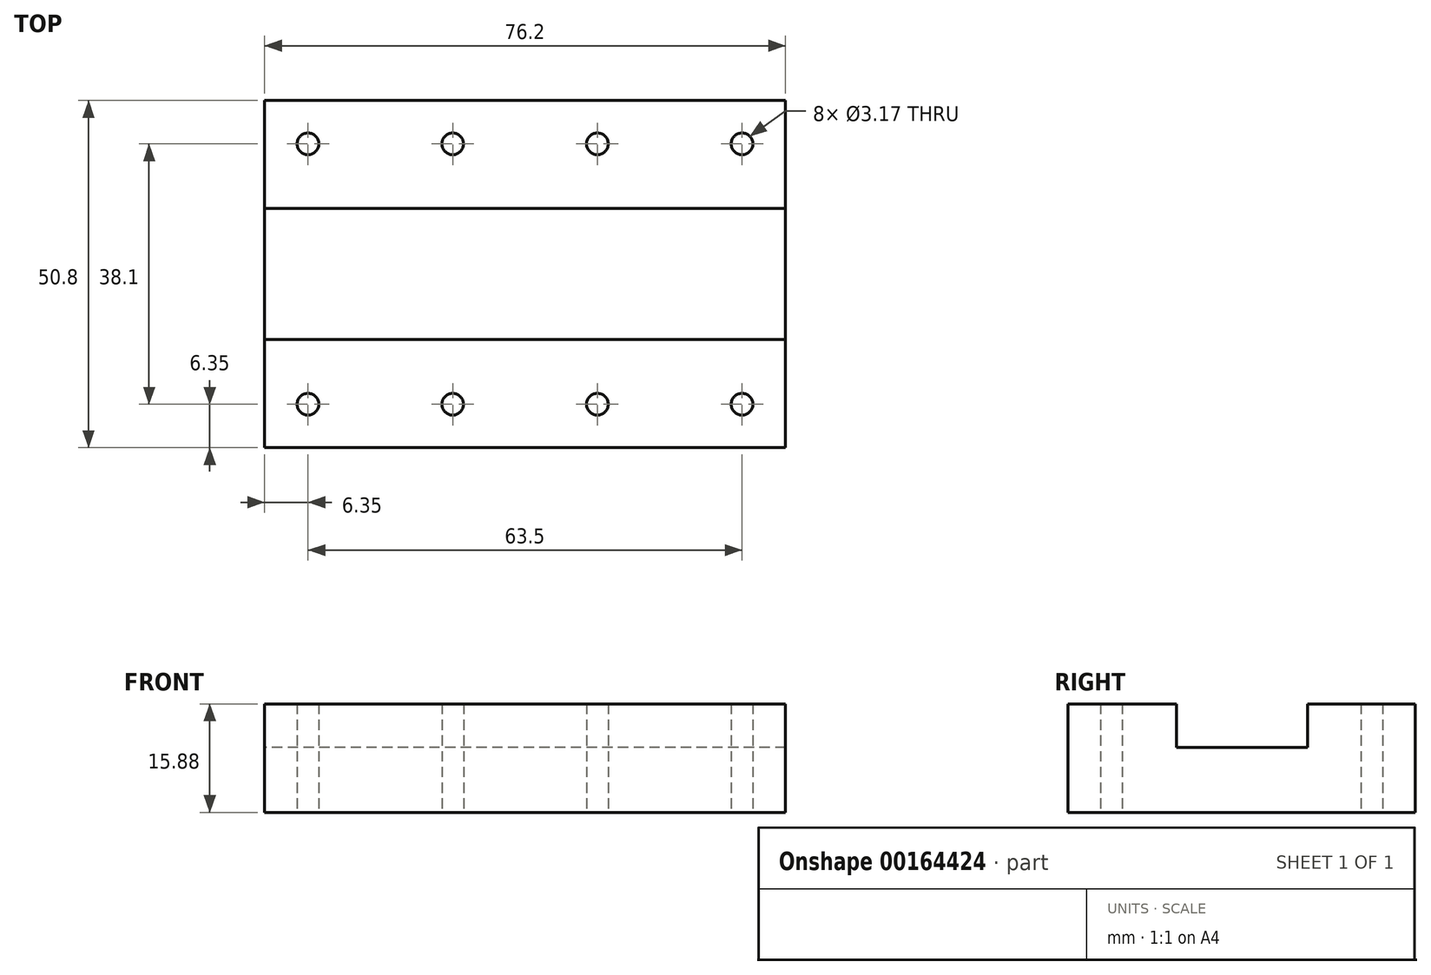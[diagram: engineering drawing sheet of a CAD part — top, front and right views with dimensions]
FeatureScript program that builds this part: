
annotation { "Feature Type Name" : "Feature", "Feature Type Description" : "" }
export const myFeature = defineFeature(function(context is Context, id is Id, definition is map)
    precondition{}
    {
        {
            var Q0;
            Q0=qCreatedBy(makeId("Top.planeOp"),FACE);
            var sketch = newSketch(context, id + "F0", { "sketchPlane" : qUnion([Q0])});
            skLineSegment(sketch, "E0.bottom", {"start": v(-38.1, -25.4) * mm, "end": v(38.1, -25.4) * mm});
            skLineSegment(sketch, "E0.top", {"start": v(-38.1, 25.4) * mm, "end": v(38.1, 25.4) * mm});
            skLineSegment(sketch, "E0.left", {"start": v(-38.1, -25.4) * mm, "end": v(-38.1, 25.4) * mm});
            skLineSegment(sketch, "E0.right", {"start": v(38.1, -25.4) * mm, "end": v(38.1, 25.4) * mm});
            skPoint(sketch, "E0.middle", {"position": v(0, 0) * mm});
            skLineSegment(sketch, "E1.bottom", {"start": v(-31.75, 19.05) * mm, "end": v(31.75, 19.05) * mm, "construction": true});
            skLineSegment(sketch, "E1.top", {"start": v(-31.75, -19.05) * mm, "end": v(31.75, -19.05) * mm, "construction": true});
            skLineSegment(sketch, "E1.left", {"start": v(-31.75, 19.05) * mm, "end": v(-31.75, -19.05) * mm, "construction": true});
            skLineSegment(sketch, "E1.right", {"start": v(31.75, 19.05) * mm, "end": v(31.75, -19.05) * mm, "construction": true});
            skCircle(sketch, "E2", {"center": v(-31.75, -19.05) * mm, "radius": 1.59 * mm});
            skCircle(sketch, "E3", {"center": v(-31.75, 19.05) * mm, "radius": 1.59 * mm});
            skCircle(sketch, "E4", {"center": v(31.75, 19.05) * mm, "radius": 1.59 * mm});
            skCircle(sketch, "E5", {"center": v(31.75, -19.05) * mm, "radius": 1.59 * mm});
            skCircle(sketch, "E6.1.0.0", {"center": v(-10.58, 19.05) * mm, "radius": 1.59 * mm});
            skCircle(sketch, "E6.1.0.1", {"center": v(-10.58, -19.05) * mm, "radius": 1.59 * mm});
            skCircle(sketch, "E6.2.0.0", {"center": v(10.58, 19.05) * mm, "radius": 1.59 * mm});
            skCircle(sketch, "E6.2.0.1", {"center": v(10.58, -19.05) * mm, "radius": 1.59 * mm});
            skLineSegment(sketch, "E6.direction1", {"start": v(-31.75, -19.05) * mm, "end": v(-10.58, -19.05) * mm, "construction": true});
            skLineSegment(sketch, "E7", {"start": v(0, 0) * mm, "end": v(-10.58, 0) * mm, "construction": true});
            skLineSegment(sketch, "E8", {"start": v(-10.58, 0) * mm, "end": v(-10.58, 19.05) * mm, "construction": true});
            skLineSegment(sketch, "E9", {"start": v(0, 0) * mm, "end": v(10.58, 0) * mm, "construction": true});
            skLineSegment(sketch, "E10", {"start": v(10.58, 0) * mm, "end": v(10.58, 19.05) * mm, "construction": true});
            skSolve(sketch);
        }
        {
            var Q0;
            Q0=makeQuery(id+"F0.imprint","IMPRINT",FACE,{"disambiguationData":[TD([[makeQuery(id+"F0.imprint","IMPRINT",EDGE,{"derivedFrom":sQuery(id+"F0.wireOp",EDGE,"E0.bottom")}),1.0]])]});
            extrude(context, id + "F1", {"entities" : qUnion([Q0]), "depth" : 15.88 * mm});
        }
        {
            var Q0;
            Q0=makeQuery(id+"F1.opExtrude","CAP_FACE",FACE,{"disambiguationData":[OSD([sQuery(id+"F0.wireOp",EDGE,"E0.bottom"),sQuery(id+"F0.wireOp",EDGE,"E0.top"),sQuery(id+"F0.wireOp",EDGE,"E0.left"),sQuery(id+"F0.wireOp",EDGE,"E0.right"),sQuery(id+"F0.wireOp",EDGE,"E2"),sQuery(id+"F0.wireOp",EDGE,"E3"),sQuery(id+"F0.wireOp",EDGE,"E4"),sQuery(id+"F0.wireOp",EDGE,"E5")])],"isStart":false});
            var sketch = newSketch(context, id + "F2", { "sketchPlane" : qUnion([Q0])});
            skLineSegment(sketch, "E11.bottom", {"start": v(38.1, 9.59) * mm, "end": v(-38.1, 9.59) * mm});
            skLineSegment(sketch, "E11.top", {"start": v(38.1, -9.59) * mm, "end": v(-38.1, -9.59) * mm});
            skLineSegment(sketch, "E11.left", {"start": v(38.1, 9.59) * mm, "end": v(38.1, -9.59) * mm});
            skLineSegment(sketch, "E11.right", {"start": v(-38.1, 9.59) * mm, "end": v(-38.1, -9.59) * mm});
            skPoint(sketch, "E11.middle", {"position": v(0, 0) * mm});
            skSolve(sketch);
        }
        {
            var Q0;
            Q0=makeQuery(id+"F2.imprint","IMPRINT",FACE,{"disambiguationData":[TD([[makeQuery(id+"F2.imprint","IMPRINT",EDGE,{"derivedFrom":sQuery(id+"F2.wireOp",EDGE,"E11.bottom")}),1.0]])]});
            extrude(context, id + "F3", {"entities" : qUnion([Q0]), "operationType" : NewBodyOperationType.REMOVE, "oppositeDirection" : true, "depth" : 6.35 * mm});
        }
    });
